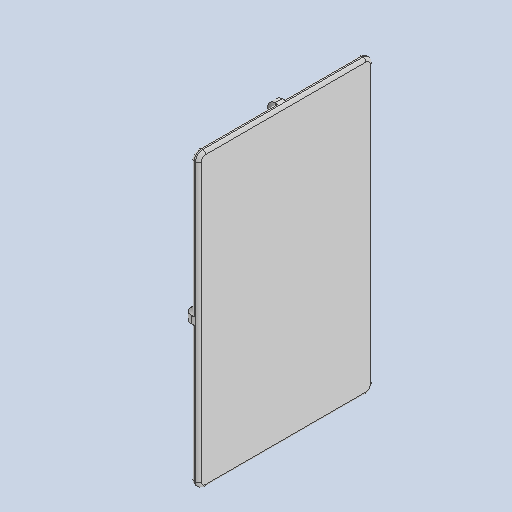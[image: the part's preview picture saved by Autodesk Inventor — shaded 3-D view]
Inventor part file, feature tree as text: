
AUTODESK INVENTOR PART (.ipt)
format: ipt  version: 2022 (Build 260153000, 153)  size: 528,896 bytes
history: native  units: mm
features: other x5, fillet x4, extrude x3, sketch x3
ambient origin geometry x8: Origin, YZ Plane, XZ Plane, XY Plane, X Axis, Y Axis, Z Axis, Center Point
bodies: Body1 (feature_tree)
feature tree (15):
  other  "Твердое тело1"
  other  "РабПлоскость1"
  extrude  "Выдавливание1"  Depth=12.0mm
  extrude  "Выдавливание2"  Depth=12.0mm
  extrude  "Выдавливание3"  Depth=16.0mm
  fillet  "Сопряжение1"  Radius=6.0mm
  fillet  "Сопряжение2"  Radius=100.0mm
  fillet  "Сопряжение3"  Radius=60.0mm
  fillet  "Сопряжение4"  Radius=30.0mm
  sketch  "Эскиз1"
  sketch  "Эскиз2"
  sketch  "Эскиз3"
  other  "<userpath>\Documents\Inventor\AIM\Aim.iam"
  other  "Aim.iam"
  other  "Fastener:1"
